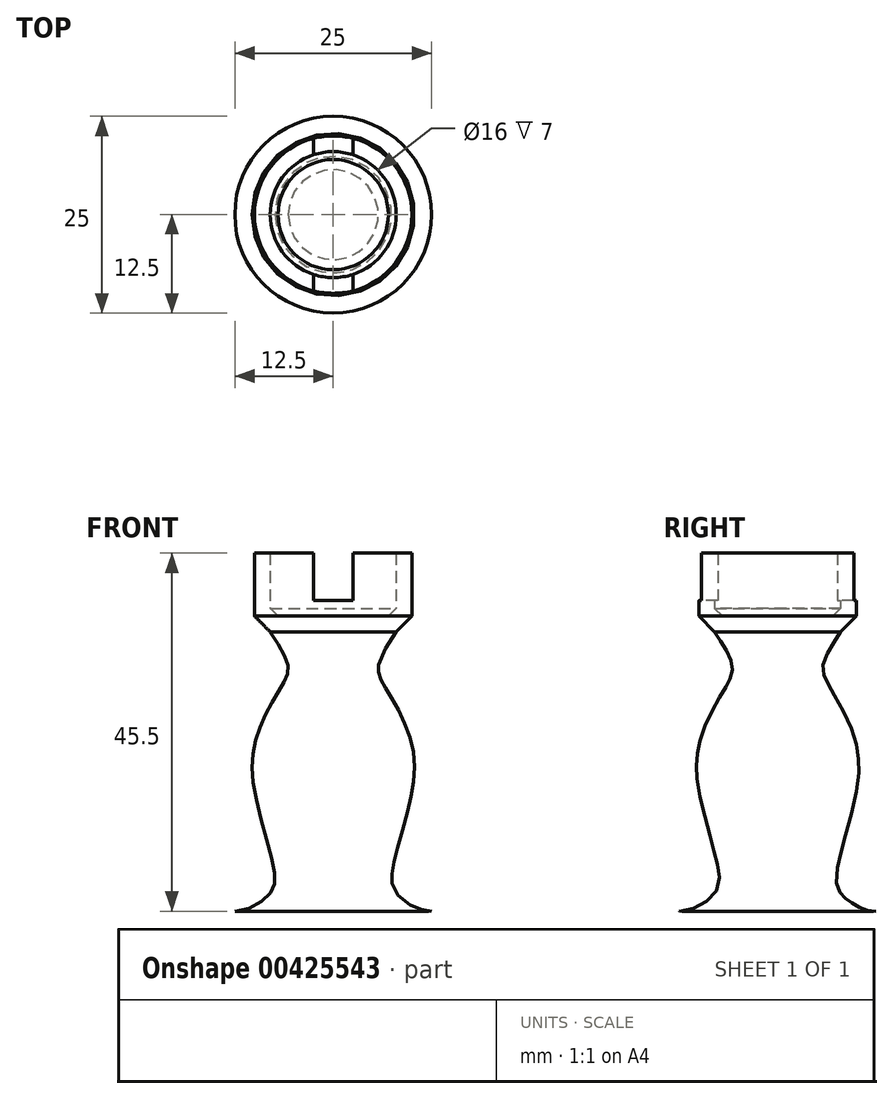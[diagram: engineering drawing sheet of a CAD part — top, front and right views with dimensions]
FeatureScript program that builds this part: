
annotation { "Feature Type Name" : "Feature", "Feature Type Description" : "" }
export const myFeature = defineFeature(function(context is Context, id is Id, definition is map)
    precondition{}
    {
        {
            var Q0;
            Q0=qCreatedBy(makeId("Front.planeOp"),FACE);
            var sketch = newSketch(context, id + "F0", { "sketchPlane" : qUnion([Q0])});
            skLineSegment(sketch, "E0.bottom", {"start": v(0, 0) * mm, "end": v(12.5, 0) * mm});
            skLineSegment(sketch, "E0.top", {"start": v(0, 48) * mm, "end": v(12.5, 48) * mm});
            skLineSegment(sketch, "E0.left", {"start": v(0, 0) * mm, "end": v(0, 48) * mm});
            skLineSegment(sketch, "E0.right", {"start": v(12.5, 0) * mm, "end": v(12.5, 48) * mm});
            skLineSegment(sketch, "E1.bottom", {"start": v(0, 48) * mm, "end": v(8, 48) * mm});
            skLineSegment(sketch, "E1.top", {"start": v(0, 40) * mm, "end": v(8, 40) * mm});
            skLineSegment(sketch, "E1.left", {"start": v(0, 48) * mm, "end": v(0, 40) * mm});
            skLineSegment(sketch, "E1.right", {"start": v(8, 48) * mm, "end": v(8, 40) * mm});
            skLineSegment(sketch, "E2.bottom", {"start": v(12.5, 0) * mm, "end": v(0, 0) * mm});
            skLineSegment(sketch, "E2.top", {"start": v(12.5, 2.5) * mm, "end": v(0, 2.5) * mm});
            skLineSegment(sketch, "E2.left", {"start": v(12.5, 0) * mm, "end": v(12.5, 2.5) * mm});
            skLineSegment(sketch, "E2.right", {"start": v(0, 0) * mm, "end": v(0, 2.5) * mm});
            skLineSegment(sketch, "E3", {"start": v(10, 48) * mm, "end": v(10, 38) * mm});
            skLineSegment(sketch, "E4", {"start": v(10, 38) * mm, "end": v(0, 38) * mm});
            skLineSegment(sketch, "E5", {"start": v(10, 40) * mm, "end": v(8, 38) * mm});
            skFitSpline(sketch, "E6", {"points": [v(8, 38) * mm, v(5.78, 33.87) * mm, v(6.07, 31.95) * mm, v(8, 28.6) * mm, v(10, 23.62) * mm, v(10, 17.77) * mm, v(7.54, 7.78) * mm, v(8, 4.8) * mm, v(12.5, 2.5) * mm], "startDerivative": vector(-23.67, -36.41) * mm, "endDerivative": vector(41.2, 0) * mm});
            skSolve(sketch);
        }
        {
            var Q0;
            {var subQ0=sQuery(id+"F0.wireOp",EDGE,"E2.top");Q0=makeQuery(id+"F0.imprint","IMPRINT",FACE,{"disambiguationData":[TD([[makeQuery(id+"F0.imprint","IMPRINT",EDGE,{"derivedFrom":subQ0}),-1.0]])]});}
            var Q1;
            {var subQ0=sQuery(id+"F0.wireOp",EDGE,"E1.top");Q1=makeQuery(id+"F0.imprint","IMPRINT",FACE,{"disambiguationData":[TD([[makeQuery(id+"F0.imprint","IMPRINT",EDGE,{"derivedFrom":subQ0}),-1.0]])]});}
            var Q2;
            Q2=makeQuery(id+"F0.imprint","IMPRINT",FACE,{"disambiguationData":[TD([[makeQuery(id+"F0.imprint","IMPRINT",EDGE,{"derivedFrom":sQuery(id+"F0.wireOp",EDGE,"E2.bottom")}),-1.0]])]});
            var Q3;
            Q3=sQuery(id+"F0.wireOp",EDGE,"E0.left");
            revolve(context, id + "F1", {"entities" : qUnion([Q0, Q1, Q2]), "axis" : qUnion([Q3]), "revolveType" : RevolveType.FULL});
        }
        {
            var Q0;
            Q0=makeQuery(id+"F1.opRevolve","SWEPT_FACE",FACE,{"disambiguationData":[OSD([sQuery(id+"F0.wireOp",EDGE,"E0.top")])]});
            var sketch = newSketch(context, id + "F2", { "sketchPlane" : qUnion([Q0])});
            skLineSegment(sketch, "E7.bottom", {"start": v(2.5, 15) * mm, "end": v(-2.5, 15) * mm});
            skLineSegment(sketch, "E7.top", {"start": v(2.5, -15) * mm, "end": v(-2.5, -15) * mm});
            skLineSegment(sketch, "E7.left", {"start": v(2.5, 15) * mm, "end": v(2.5, -15) * mm});
            skLineSegment(sketch, "E7.right", {"start": v(-2.5, 15) * mm, "end": v(-2.5, -15) * mm});
            skPoint(sketch, "E7.middle", {"position": v(0, 0) * mm});
            skSolve(sketch);
        }
        {
            var Q0;
            Q0 = qSketchRegion(id + "F2", true);
            extrude(context, id + "F3", {"entities" : qUnion([Q0]), "operationType" : NewBodyOperationType.REMOVE, "oppositeDirection" : true, "depth" : 6 * mm});
        }
        {
            var Q0;
            Q0=makeQuery(id+"F1.opRevolve","SWEPT_FACE",FACE,{"disambiguationData":[OSD([sQuery(id+"F0.wireOp",EDGE,"E1.top")])]});
            chamfer(context, id + "F4", {"entities" : qUnion([Q0]), "width" : 1 * mm, "tangentPropagation" : true});
        }
    });
